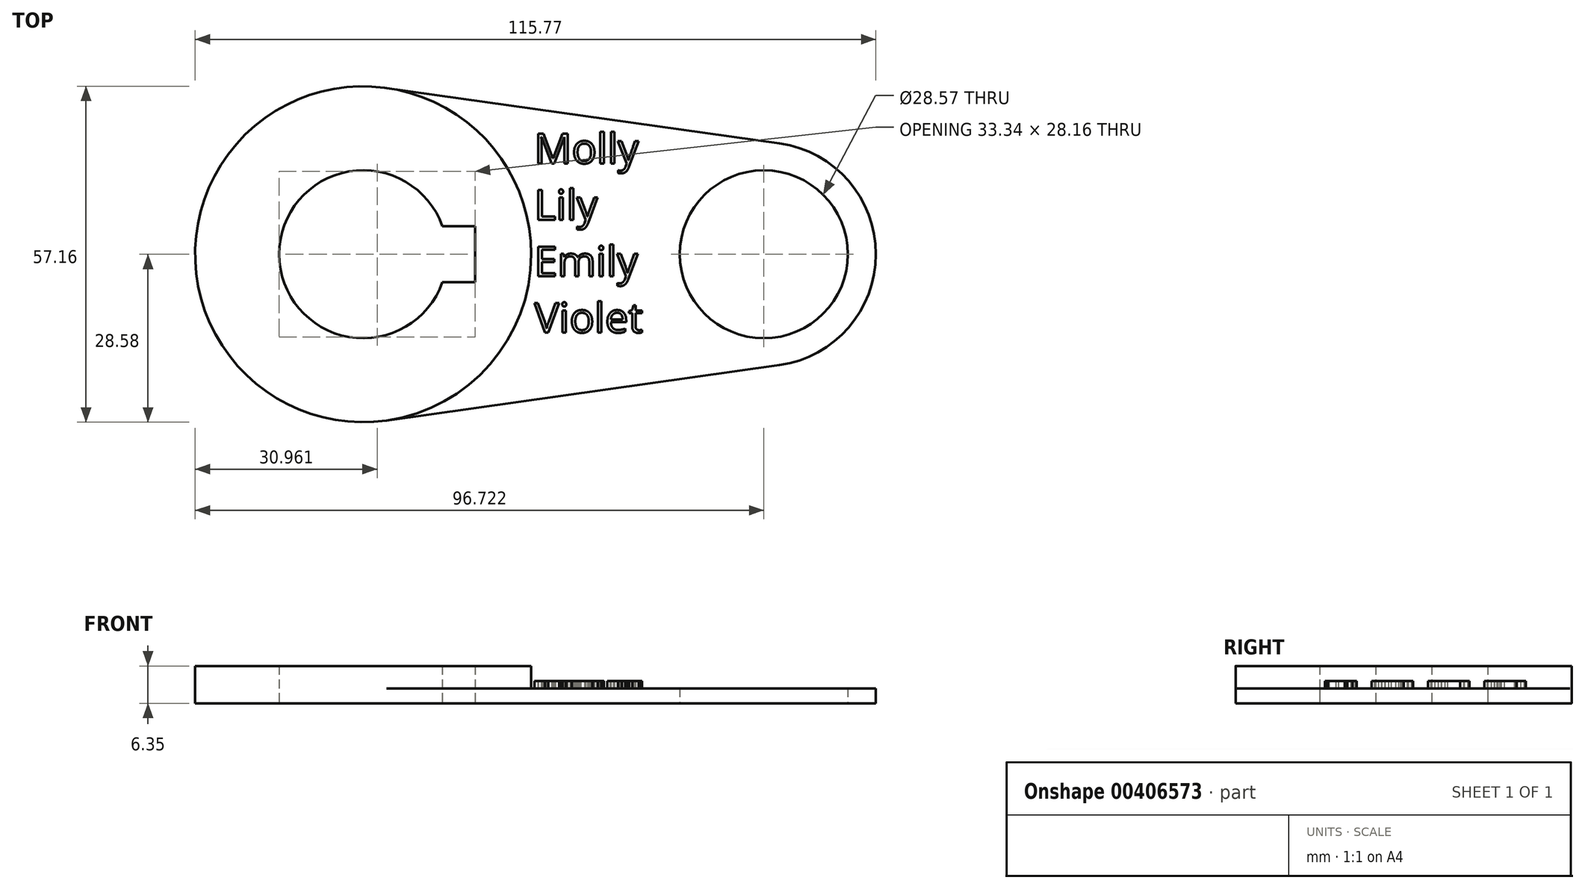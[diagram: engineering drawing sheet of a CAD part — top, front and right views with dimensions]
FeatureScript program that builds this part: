
annotation { "Feature Type Name" : "Feature", "Feature Type Description" : "" }
export const myFeature = defineFeature(function(context is Context, id is Id, definition is map)
    precondition{}
    {
        {
            var Q0;
            Q0=qCreatedBy(makeId("Top.planeOp"),FACE);
            var sketch = newSketch(context, id + "F0", { "sketchPlane" : qUnion([Q0])});
            skCircle(sketch, "E0", {"center": v(0, 0) * mm, "radius": 28.58 * mm});
            skCircle(sketch, "E1", {"center": v(68.14, 0) * mm, "radius": 19.05 * mm});
            skLineSegment(sketch, "E2", {"start": v(4, 28.3) * mm, "end": v(70.8, 18.86) * mm});
            skLineSegment(sketch, "E3", {"start": v(4, -28.3) * mm, "end": v(70.8, -18.86) * mm});
            skCircle(sketch, "E4", {"center": v(0, 0) * mm, "radius": 14.29 * mm});
            skCircle(sketch, "E5", {"center": v(68.14, 0) * mm, "radius": 14.29 * mm});
            skLineSegment(sketch, "E6.bottom", {"start": v(19.05, 4.76) * mm, "end": v(-19.05, 4.76) * mm});
            skLineSegment(sketch, "E6.top", {"start": v(19.05, -4.76) * mm, "end": v(-19.05, -4.76) * mm});
            skLineSegment(sketch, "E6.left", {"start": v(19.05, 4.76) * mm, "end": v(19.05, -4.76) * mm});
            skLineSegment(sketch, "E6.right", {"start": v(-19.05, 4.76) * mm, "end": v(-19.05, -4.76) * mm});
            skSolve(sketch);
        }
        {
            var Q0;
            {var subQ7=sQuery(id+"F0.wireOp",EDGE,"E6.left");Q0=makeQuery(id+"F0.imprint","IMPRINT",FACE,{"disambiguationData":[TD([[makeQuery(id+"F0.imprint","IMPRINT",EDGE,{"derivedFrom":subQ7}),1.0]])]});}
            var Q1;
            {var subQ5=sQuery(id+"F0.wireOp",EDGE,"E6.right");Q1=makeQuery(id+"F0.imprint","IMPRINT",FACE,{"disambiguationData":[TD([[makeQuery(id+"F0.imprint","IMPRINT",EDGE,{"derivedFrom":subQ5}),1.0]])]});}
            var Q2;
            {var subQ0=sQuery(id+"F0.wireOp",EDGE,"E2");Q2=makeQuery(id+"F0.imprint","IMPRINT",FACE,{"disambiguationData":[TD([[makeQuery(id+"F0.imprint","IMPRINT",EDGE,{"derivedFrom":subQ0}),-1.0]])]});}
            var Q3;
            Q3=makeQuery(id+"F0.imprint","IMPRINT",FACE,{"disambiguationData":[TD([[makeQuery(id+"F0.imprint","IMPRINT",EDGE,{"derivedFrom":sQuery(id+"F0.wireOp",EDGE,"E5")}),-1.0]])]});
            extrude(context, id + "F1", {"entities" : qUnion([Q0, Q1, Q2, Q3]), "depth" : 2.54 * mm});
        }
        {
            var Q0;
            {var subQ7=sQuery(id+"F0.wireOp",EDGE,"E6.left");Q0=makeQuery(id+"F0.imprint","IMPRINT",FACE,{"disambiguationData":[TD([[makeQuery(id+"F0.imprint","IMPRINT",EDGE,{"derivedFrom":subQ7}),1.0]])]});}
            var Q1;
            {var subQ5=sQuery(id+"F0.wireOp",EDGE,"E6.right");Q1=makeQuery(id+"F0.imprint","IMPRINT",FACE,{"disambiguationData":[TD([[makeQuery(id+"F0.imprint","IMPRINT",EDGE,{"derivedFrom":subQ5}),1.0]])]});}
            extrude(context, id + "F2", {"entities" : qUnion([Q0, Q1]), "operationType" : NewBodyOperationType.ADD, "depth" : 6.35 * mm});
        }
        {
            var Q0;
            Q0=makeQuery(id+"F1.opExtrude","CAP_FACE",FACE,{"disambiguationData":[OSD([sQuery(id+"F0.wireOp",EDGE,"E0"),sQuery(id+"F0.wireOp",EDGE,"E1"),sQuery(id+"F0.wireOp",EDGE,"E2"),sQuery(id+"F0.wireOp",EDGE,"E3"),sQuery(id+"F0.wireOp",EDGE,"E4"),sQuery(id+"F0.wireOp",EDGE,"E5"),sQuery(id+"F0.wireOp",EDGE,"E6.bottom"),sQuery(id+"F0.wireOp",EDGE,"E6.top"),sQuery(id+"F0.wireOp",EDGE,"E6.left")])],"isStart":false});
            var sketch = newSketch(context, id + "F3", { "sketchPlane" : qUnion([Q0])});
            skText(sketch, "E7", { "text": "Molly\nLily\nEmily\nViolet", "fontName": "OpenSans-Regular.ttf"});
            const initialGuessF3  = {"E7": [0.0291, 0.01546, 1, 0, 0.00508]};
            skSetInitialGuess(sketch, initialGuessF3);
            skSolve(sketch);
        }
        {
            var Q0;
            Q0 = qSketchRegion(id + "F3", true);
            extrude(context, id + "F4", {"entities" : qUnion([Q0]), "operationType" : NewBodyOperationType.ADD, "depth" : 1.27 * mm});
        }
    });
